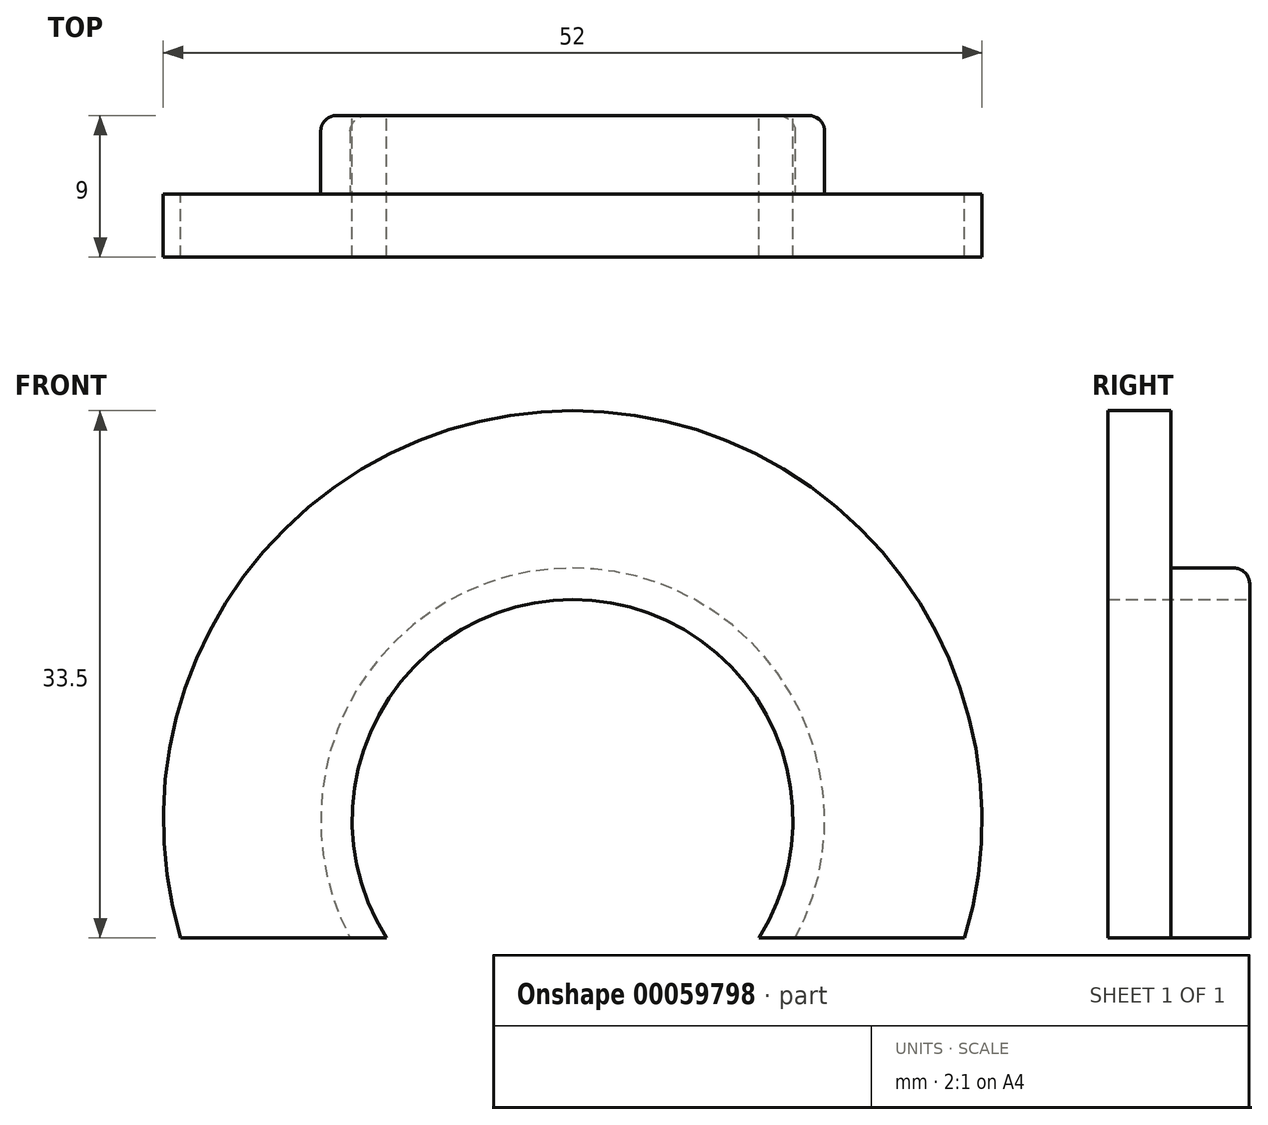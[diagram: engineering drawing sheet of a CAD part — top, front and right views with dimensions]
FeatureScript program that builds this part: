
annotation { "Feature Type Name" : "Feature", "Feature Type Description" : "" }
export const myFeature = defineFeature(function(context is Context, id is Id, definition is map)
    precondition{}
    {
        {
            var Q0;
            Q0=qCreatedBy(makeId("Front.planeOp"),FACE);
            var sketch = newSketch(context, id + "F0", { "sketchPlane" : qUnion([Q0])});
            skLineSegment(sketch, "E0", {"start": v(0, 0) * mm, "end": v(0, 7.5) * mm, "construction": true});
            skLineSegment(sketch, "E1", {"start": v(-100.93, 0) * mm, "end": v(99.07, 0) * mm, "construction": true});
            skCircle(sketch, "E2", {"center": v(0, 7.5) * mm, "radius": 16 * mm, "construction": true});
            skCircle(sketch, "E3", {"center": v(0, 7.5) * mm, "radius": 26 * mm, "construction": true});
            skLineSegment(sketch, "E4", {"start": v(0, 7.5) * mm, "end": v(0, 23.5) * mm, "construction": true});
            skArc(sketch, "E5", {"start": v(24.9, 0) * mm, "mid": v(0, 33.5) * mm, "end": v(-24.9, 0) * mm});
            skCircle(sketch, "E6", {"center": v(0, 7.5) * mm, "radius": 14 * mm, "construction": true});
            skArc(sketch, "E7", {"start": v(-11.82, 0) * mm, "mid": v(0, 21.5) * mm, "end": v(11.82, 0) * mm});
            skLineSegment(sketch, "E8", {"start": v(-11.82, 0) * mm, "end": v(-24.9, 0) * mm});
            skLineSegment(sketch, "E9", {"start": v(11.82, 0) * mm, "end": v(24.9, 0) * mm});
            skSolve(sketch);
        }
        {
            var Q0;
            Q0=qSketchRegion(id+"F0",true);
            extrude(context, id + "F1", {"entities" : qUnion([Q0]), "depth" : 4 * mm});
        }
        {
            var Q0;
            Q0=makeQuery(id+"F1.opExtrude","CAP_FACE",FACE,{"disambiguationData":[OSD([sQuery(id+"F0.wireOp",EDGE,"E5"),sQuery(id+"F0.wireOp",EDGE,"E7"),sQuery(id+"F0.wireOp",EDGE,"E8"),sQuery(id+"F0.wireOp",EDGE,"E9")])],"isStart":true});
            var sketch = newSketch(context, id + "F2", { "sketchPlane" : qUnion([Q0])});
            skCircle(sketch, "E10", {"center": v(0, 7.5) * mm, "radius": 14 * mm, "construction": true});
            skCircle(sketch, "E11", {"center": v(0, 7.5) * mm, "radius": 16 * mm, "construction": true});
            skLineSegment(sketch, "E12", {"start": v(-11.82, 0) * mm, "end": v(-14.13, 0) * mm});
            skLineSegment(sketch, "E13", {"start": v(11.82, 0) * mm, "end": v(14.13, 0) * mm});
            skArc(sketch, "E14", {"start": v(-14.13, 0) * mm, "mid": v(0, 23.5) * mm, "end": v(14.13, 0) * mm});
            skArc(sketch, "E15", {"start": v(-11.82, 0) * mm, "mid": v(0, 21.5) * mm, "end": v(11.82, 0) * mm});
            skSolve(sketch);
        }
        {
            var Q0;
            Q0=qSketchRegion(id+"F2",true);
            extrude(context, id + "F3", {"entities" : qUnion([Q0]), "operationType" : NewBodyOperationType.ADD, "depth" : 5 * mm});
        }
        {
            var Q0;
            Q0=makeQuery(id+"F3.opExtrude","CAP_EDGE",EDGE,{"disambiguationData":[OSD([sQuery(id+"F2.wireOp",EDGE,"E14")])],"isStart":false});
            fillet(context, id + "F4", {"entities" : qUnion([Q0]), "radius" : 1 * mm, "tangentPropagation" : true, "allowEdgeOverflow" : false});
        }
    });
